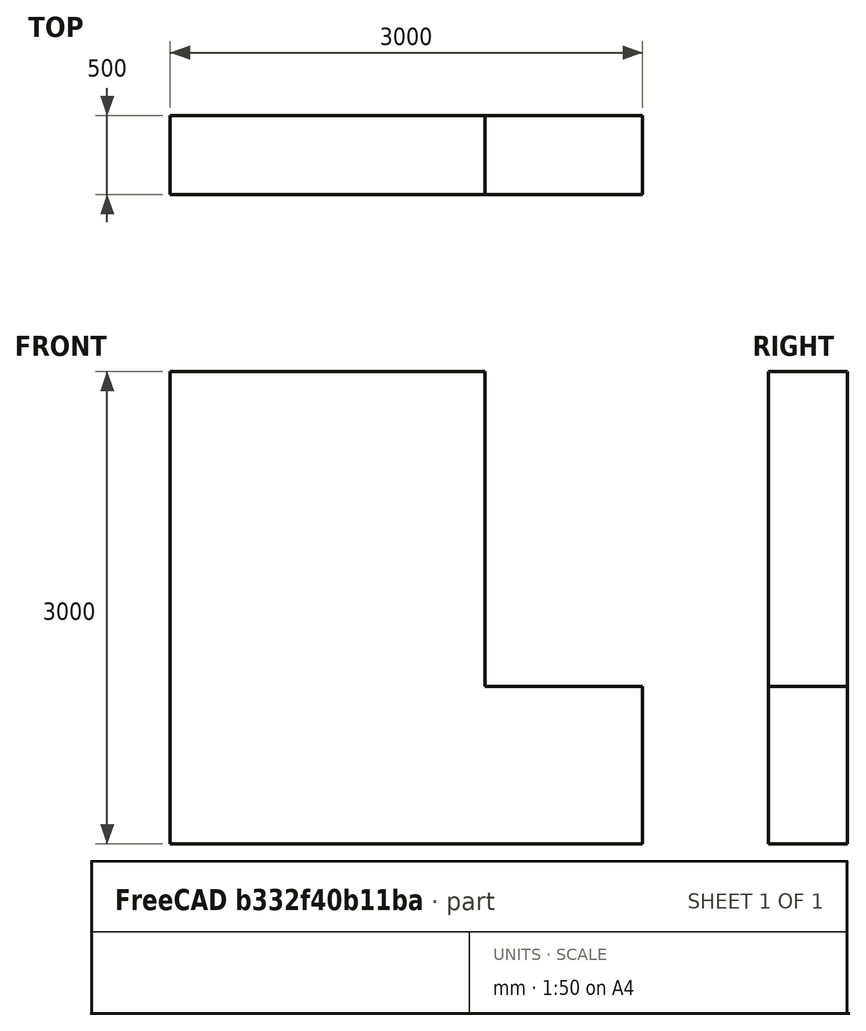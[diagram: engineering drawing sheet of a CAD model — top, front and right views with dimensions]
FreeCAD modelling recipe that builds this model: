
FCSTD DOCUMENT  (FreeCAD 0.21R33694 (Git))
Label: Trench_Example
License: All rights reserved
LicenseURL: http://en.wikipedia.org/wiki/All_rights_reserved
objects: Sketcher::SketchObject×1, PartDesign::Pad×1, PartDesign::Body×1, Fem::FemSolverObjectPython×1, Fem::FemMeshObjectPython×1, App::MaterialObjectPython×1, Fem::ConstraintFixed×1, Fem::ConstraintDisplacement×1, Fem::FemAnalysis×1
note: 4 computed .brp shape members not serialized (recipe doc carries the construction recipe); baked Part::Feature solids carry a one-line shape summary decoded from their .brp

FEATURE [Sketcher::SketchObject] Sketch
  FullyConstrained = true
  MapMode = 5
  Placement = pos=(0,0,0) rot=(1,0,0;1.5708rad)
  Support = -> [XZ_Plane]
  sketch-geometry (6):
    g0: LineSegment StartX=0 StartY=0 StartZ=0 EndX=3000 EndY=0 EndZ=0
    g1: LineSegment StartX=0 StartY=0 StartZ=0 EndX=0 EndY=3000 EndZ=0
    g2: LineSegment StartX=0 StartY=3000 StartZ=0 EndX=2000 EndY=3000 EndZ=0
    g3: LineSegment StartX=2000 StartY=3000 StartZ=0 EndX=2000 EndY=1000 EndZ=0
    g4: LineSegment StartX=2000 StartY=1000 StartZ=0 EndX=3000 EndY=1000 EndZ=0
    g5: LineSegment StartX=3000 StartY=1000 StartZ=0 EndX=3000 EndY=0 EndZ=0
  constraints (18):
    c: Coincident(g0,g-1)
    c: Horizontal(g0)
    c: Distance(g0) = 3000
    c: Coincident(g1,g0)
    c: PointOnObject(g1,g-2)
    c: Coincident(g2,g1)
    c: Horizontal(g2)
    c: Coincident(g3,g2)
    c: Vertical(g3)
    c: Horizontal(g4)
    c: Coincident(g5,g0)
    c: Distance(g2) = 2000
    c: Distance(g4) = 1000
    c: Distance(g5) = 1000
    c: Distance(g1) = 3000
    c: Distance(g3) = 2000
    c: Coincident(g3,g4)
    c: Vertical(g5)
FEATURE [PartDesign::Pad] Pad
  Direction = (0,-1,-2e-16)
  Length = 500
  Length2 = 10
  Placement = pos=(0,0,0) rot=(1,0,0;1.5708rad)
  Profile = -> Sketch
  ReferenceAxis = -> Sketch [N_Axis]
  Type = 0
FEATURE [PartDesign::Body] Body
  Group = -> [Sketch,Pad]
  Origin = -> Origin
  Tip = -> Pad
FEATURE [Fem::FemSolverObjectPython] SolverCcxTools  # FEM object (typed FeaturePython)
  AnalysisType = 0
  BeamShellResultOutput3D = false
  BucklingFactors = 1
  EigenmodeHighLimit = 1000000
  EigenmodeLowLimit = 0
  EigenmodesCount = 10
  GeometricalNonlinearity = 0
  IterationsControlParameterCutb = 0.25,0.5,0.75,0.85,,,1.5,
  IterationsControlParameterIter = 4,8,9,200,10,400,,200,,
  IterationsControlParameterTimeUse = false
  IterationsThermoMechMaximum = 2000
  IterationsUserDefinedIncrementations = false
  IterationsUserDefinedTimeStepLength = false
  MaterialNonlinearity = 0
  MatrixSolverType = 0
  SplitInputWriter = false
  ThermoMechSteadyState = true
  TimeEnd = 1
  TimeInitialStep = 0.01
FEATURE [Fem::FemMeshObjectPython] FEMMeshGmsh  # FEM object (typed FeaturePython)
  Algorithm2D = 0
  Algorithm3D = 0
  CharacteristicLengthMax = 0
  CharacteristicLengthMin = 0
  CoherenceMesh = true
  ElementDimension = 0
  ElementOrder = 1
  GeometryTolerance = 1e-06
  GroupsOfNodes = false
  HighOrderOptimize = 0
  MeshSizeFromCurvature = 12
  OptimizeNetgen = false
  OptimizeStd = true
  Part = -> Body
  RecombinationAlgorithm = 0
  Recombine3DAll = false
  RecombineAll = false
  SecondOrderLinear = false
FEATURE [App::MaterialObjectPython] MaterialSolid  # material (typed FeaturePython)
  Category = 0
  Material = Density=2000.0000000000002 kg/m^3; Name=NoName; PoissonRatio=0.45; YoungsModulus=5000.0 kPa
  References = -> [Pad]
FEATURE [Fem::ConstraintFixed] ConstraintFixed
  NormalDirection = (-1,0,0)
  Normals = (80) [(-1,0,0),(-1,0,0),(-1,0,0),(-1,0,0),(-1,0,0),(-1,0,0),(-1,0,0),(-1,0,0),(-1,0,0),(-1,0,0),(-1,0,0),(-1,0,0),(-1,0,0),(-1,0,0),(-1,0,0),(-1,0,0),+64 more]
  Points = (80) [(0,-500,0),(0,-500,428.571),(0,-500,857.143),(0,-500,1285.71),(0,-500,1714.29),(0,-500,2142.86),(0,-500,2571.43),(0,-500,3000),(0,-333.333,0),+71 more]
  References = -> [Pad]
  Scale = 29
FEATURE [Fem::ConstraintDisplacement] ConstraintDisplacement
  NormalDirection = (0,-1,-2e-16)
  Normals = (82) [(0,-1,-2.2e-16),(0,-1,-2.2e-16),(0,-1,-2.2e-16),(0,-1,-2.2e-16),(0,-1,-2.2e-16),(0,-1,-2.2e-16),(0,-1,-2.2e-16),(0,-1,-2.2e-16),(0,-1,-2.2e-16),+73 more]
  Points = (82) [(0,-500,0),(0,-500,500),(0,-500,1000),(0,-500,1500),(0,-500,2000),(0,-500,2500),(0,-500,3000),(500,-500,0),(500,-500,500),(500,-500,1000),+72 more]
  References = -> [Pad]
  Scale = 51
  hasXFormula = false
  hasYFormula = false
  hasZFormula = false
  rotxFix = false
  rotxFree = true
  rotyFix = false
  rotyFree = true
  rotzFix = false
  rotzFree = true
  useFlowSurfaceForce = false
  xDisplacement = 0
  xFix = false
  xFree = true
  xRotation = 0
  yDisplacement = 0
  yFix = true
  yFree = false
  yRotation = 0
  zDisplacement = 0
  zFix = false
  zFree = true
  zRotation = 0
FEATURE [Fem::FemAnalysis] Analysis
  Group = -> [SolverCcxTools,FEMMeshGmsh,MaterialSolid,ConstraintFixed,ConstraintDisplacement]
